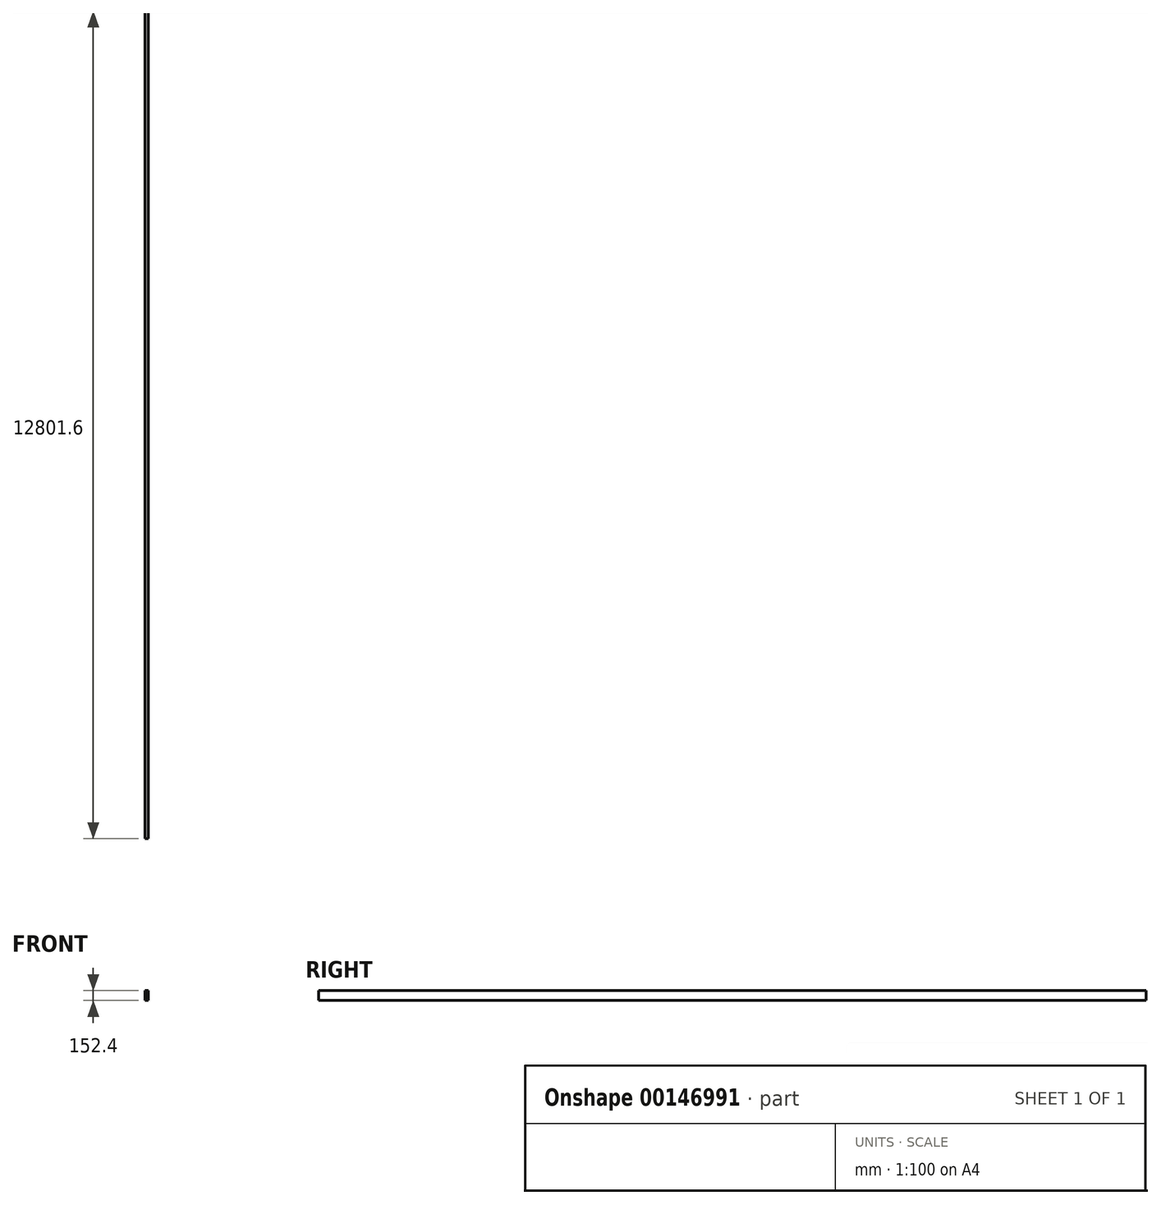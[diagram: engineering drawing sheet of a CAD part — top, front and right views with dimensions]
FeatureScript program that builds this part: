
annotation { "Feature Type Name" : "Feature", "Feature Type Description" : "" }
export const myFeature = defineFeature(function(context is Context, id is Id, definition is map)
    precondition{}
    {
        {
            var Q0;
            Q0=qCreatedBy(makeId("Front.planeOp"),FACE);
            var sketch = newSketch(context, id + "F0", { "sketchPlane" : qUnion([Q0])});
            skLineSegment(sketch, "E0.bottom", {"start": v(0, 0) * mm, "end": v(50.8, 0) * mm});
            skLineSegment(sketch, "E0.top", {"start": v(0, 152.4) * mm, "end": v(50.8, 152.4) * mm});
            skLineSegment(sketch, "E0.left", {"start": v(0, 0) * mm, "end": v(0, 152.4) * mm});
            skLineSegment(sketch, "E0.right", {"start": v(50.8, 0) * mm, "end": v(50.8, 152.4) * mm});
            skLineSegment(sketch, "E1.bottom", {"start": v(4.76, 4.76) * mm, "end": v(46.04, 4.76) * mm});
            skLineSegment(sketch, "E1.top", {"start": v(4.76, 147.64) * mm, "end": v(46.04, 147.64) * mm});
            skLineSegment(sketch, "E1.left", {"start": v(4.76, 4.76) * mm, "end": v(4.76, 147.64) * mm});
            skLineSegment(sketch, "E1.right", {"start": v(46.04, 4.76) * mm, "end": v(46.04, 147.64) * mm});
            skSolve(sketch);
        }
        {
            var Q0;
            Q0=makeQuery(id+"F0.imprint","IMPRINT",FACE,{"disambiguationData":[TD([[makeQuery(id+"F0.imprint","IMPRINT",EDGE,{"derivedFrom":sQuery(id+"F0.wireOp",EDGE,"E0.bottom")}),1.0]])]});
            extrude(context, id + "F1", {"entities" : qUnion([Q0]), "oppositeDirection" : true, "depth" : 12801.6 * mm});
        }
    });
